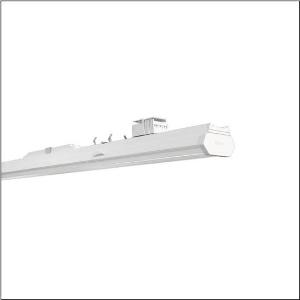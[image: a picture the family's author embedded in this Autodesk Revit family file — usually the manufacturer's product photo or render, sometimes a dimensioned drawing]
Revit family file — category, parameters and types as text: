
# Revit family: licross_r__11_protected_mo_51td127n485g_dbd9
name_source: partatom
category: Lighting Fixtures
units: mm (PartAtom-declared; Revit-internal decimal feet)

## family parameters
Cut with Voids When Loaded = No
Host = Face
Light Source = No
Part Type = Normal
Room Calculation Point = No
Round Connector Dimension = Use Diameter
Shared = No

## types (1)
- Licross® 11 Protected MO (1 x LED, 8720 lm, 48.6 W, 4000K)
    Apparent Load = 49 VA
    CIE Flux Codes = 73 92 98 99 100
    Color Rendering = 80
    Color Temperature = 4000K
    Default Elevation = 1800 mm
    Description = Licross® 11 Protected MO, luminaire insert, of sheet steel, galvanised, coil coated, white, length: 1.500mm, width: 90mm, height: 101mm, LED rated luminous flux: 8.720lm, light colour: 840, SDCM (Standard Deviation of Colour Matching)MacAdam ≤ 2 SDCM (initial), control gear: ON/OFF, with plug, 3-pole, with phase selection, mains connection: 220..240V, AC, 50/60Hz, rated input power: 49W, internal wiring halogen-free, primary light control with lens, of plastic, primary optical cover: cover, of PMMA, light emission: direct distribution, primary light characteristic: symmetric, protection rating (complete): IP54, insulation class (complete): insulation class I (protective earthing), certification: CE, ENEC, VDE, UKCA, protection symbol: D if used in an environment with non-conductive dust loads with corresponding accessories, impact resistance: IK06, permissible ambient temperature for indoor applications: -25..+35°C, corresponds to IFS (International Featured Standards) requirements for safety and quality in the food industry, reducing of maximum allowable ambient temperature of 5°C with ceiling mounting, LABS conformity tested according to VDMA 24364:2018-05, packaging unit: 1 piece
    Height = 92 mm
    Lamp = 1 x LED
    Lamp Light Flux = 8720 lm
    Lamp Power = 48.6 W
    Lamp count = 1
    Length = 1500 mm
    Luminous efficacy = 179 lm/W
    Manufacturer = Siteco
    ModVariant = No
    Model = 51TD127N485G
    Mounting Place = Ceiling
    Mounting Type = Pendant
    Number of Poles = 1
    OnlyDefault = Yes
    Power Factor = 1
    Product Name = Licross® 11 Protected MO
    Product group = luminaire insert | ceiling pendant
    ProductGroupID = 901
    Protection Class = Protection class I
    Protection Degree = IP 54
    RLX_Detail_Level = 1
    RLX_Emergency_Light_Flux = 0 lm
    RLX_Emergency_Type = 0
    RLX_Emergency_Type_DB = No
    RlxData = <blob elided: 20857 chars, md5=6a7e27f4>
    Socket = socket
    Standby Power = 0 W
    System Light Flux = 8720 lm
    System Power = 49 W
    Type Comments = Product without accessories
    Type Image = l_1256145.jpg
    URL = http://relux.com
    VarID = ---
    Voltage = 0 V
    Weight = 0.00 kg
    Width = 88 mm

## geometry (parser evidence)
native form markers: Blend x4, Sweep x10
no freeform markers — native parametric forms only
